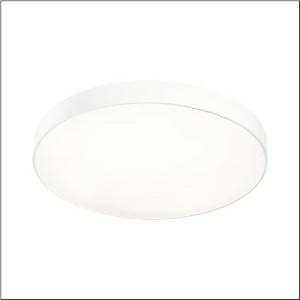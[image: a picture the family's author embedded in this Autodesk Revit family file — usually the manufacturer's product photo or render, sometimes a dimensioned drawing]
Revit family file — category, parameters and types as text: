
# Revit family: round_21_l_51mr38fd0321w
name_source: partatom
category: Lighting Fixtures
units: mm (PartAtom-declared; Revit-internal decimal feet)

## family parameters
Cut with Voids When Loaded = No
Host = Face
Light Source = No
Part Type = Normal
Room Calculation Point = No
Round Connector Dimension = Use Diameter
Shared = No

## types (1)
- Round 21 L (1 x LED, 13590 lm, 97 W, 3000K)
    Apparent Load = 97 VA
    CIE Flux Codes = 49 80 96 100 100
    Color Rendering = 80
    Color Temperature = 3000K
    Default Elevation = 1800 mm
    Description = Round 21 L, wall and ceiling luminaire, primary optical cover: cover, of PMMA, opal, light emission: direct distribution, primary light characteristic: symmetric, installation type: suspended mounting, surface-mounted, LED, rated luminous flux: 13.590lm, luminous efficacy: 140lm/W, light colour: 830, colour temperature: 3000K, control gear: DALI 2, with terminal, 5-pole, mains connection: 230V, AC, 50/60Hz, rated input power: 97W, housing, of aluminium, coated, white, diameter: 850mm, height: 62mm, protection rating (complete): IP40, insulation class (complete): insulation class I (protective earthing), certification: CE, impact resistance: IK04, permissible operating ambient temperature: -10..+35°C, packaging unit: 1 piece
    Height = 87 mm
    Lamp = 1 x LED
    Lamp Light Flux = 13590 lm
    Lamp Power = 97 W
    Lamp count = 1
    Length = 850 mm
    Luminous efficacy = 140 lm/W
    Manufacturer = Siteco
    ModVariant = No
    Model = 51MR38FD0321W
    Mounting Place = Ceiling
    Mounting Type = Surface mounted
    Number of Poles = 1
    OnlyDefault = Yes
    Power Factor = 1
    Product Name = Round 21 L
    Product group = wall and ceiling luminaire
    ProductGroupID = 304
    Protection Class = Protection class I
    Protection Degree = IP 40
    RLX_Detail_Level = 1
    RLX_Emergency_Light_Flux = 0 lm
    RLX_Emergency_Type = 0
    RLX_Emergency_Type_DB = No
    RlxData = <blob elided: 15013 chars, md5=c1380d18>
    Socket = socket
    Standby Power = 0 W
    System Light Flux = 13590 lm
    System Power = 97 W
    Type Comments = Product without accessories
    Type Image = l_1258320.jpg
    URL = http://relux.com
    VarID = ---
    Voltage = 0 V
    Weight = 0.00 kg
    Width = 0 mm  [stored 0 ft]

note: [stored X ft] marks values corroborated as IEEE doubles in the binary element streams (Revit-internal decimal feet)

## geometry (parser evidence)
native form markers: Sweep x9
no freeform markers — native parametric forms only
